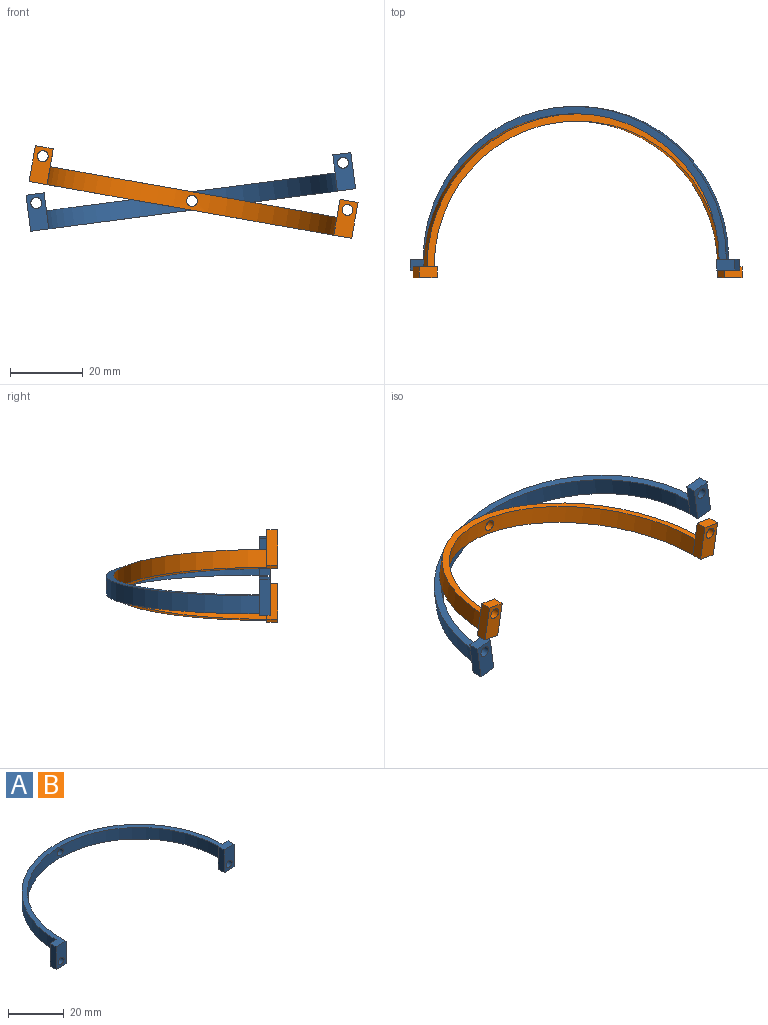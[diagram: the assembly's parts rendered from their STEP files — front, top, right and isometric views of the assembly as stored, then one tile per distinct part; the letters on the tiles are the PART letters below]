
ASSEMBLY  parts=2 mates=1
PART A: 17 faces, bbox 90x45x10 mm
  f0: cylinder r=42mm len=84mm, axis (0,0,-1), area 652.7mm2, adj f2,f3,f4,f9,f16
  f1: cylinder r=40mm len=80mm, axis (0,0,-1), area 621.2mm2, adj f2,f3,f5,f10,f16
  f2: plane 90x45mm, normal (0,0,1), area 287.6mm2, adj f0,f1,f4,f5,f6,f8,f9,f10
  f3: plane 84x42mm, normal (0,0,-1), area 257.6mm2, adj f0,f1,f4,f9
  f4: plane 10x5mm, normal (0,1,0), area 32.9mm2, adj f0,f2,f3,f5,f6,f7,f15
  f5: plane 10x3mm, normal (1,0,0), area 30mm2, adj f1,f2,f4,f7,f8
  f6: plane 10x3mm, normal (-1,0,0), area 30mm2, adj f2,f4,f7,f8
  f7: plane 5x3mm, normal (0,0,-1), area 15mm2, adj f4,f5,f6,f8
  f8: plane 10x5mm, normal (0,-1,0), area 42.9mm2, adj f2,f5,f6,f7,f15
  f9: plane 10x5mm, normal (0,1,0), area 32.9mm2, adj f0,f2,f3,f10,f11,f12,f14
  f10: plane 10x3mm, normal (-1,0,0), area 30mm2, adj f1,f2,f9,f11,f13
  f11: plane 5x3mm, normal (0,0,-1), area 15mm2, adj f9,f10,f12,f13
  f12: plane 10x3mm, normal (1,0,0), area 30mm2, adj f2,f9,f11,f13
  f13: plane 10x5mm, normal (0,-1,0), area 42.9mm2, adj f2,f10,f11,f12,f14
  f14: cylinder r=1.5mm len=3mm, axis (0,1,0), area 28.3mm2, adj f9,f13
  f15: cylinder r=1.5mm len=3mm, axis (0,1,0), area 28.3mm2, adj f4,f8
  f16: cylinder r=1.5mm len=3mm, axis (0,-1,0), area 18.9mm2, adj f0,f1
PART B: same geometry as A
PLACE A rot(axis=(0,1,0),172.5deg) t=(-195.36,-77.61,-6.12)mm
PLACE B rot(axis=(0,-1,0),170deg) t=(-193.94,-79.66,24.15)mm
MATE revolute A.f16 <-> B.f16  axis (0,-1,0) through (-96.11,15.84,4.36)mm
